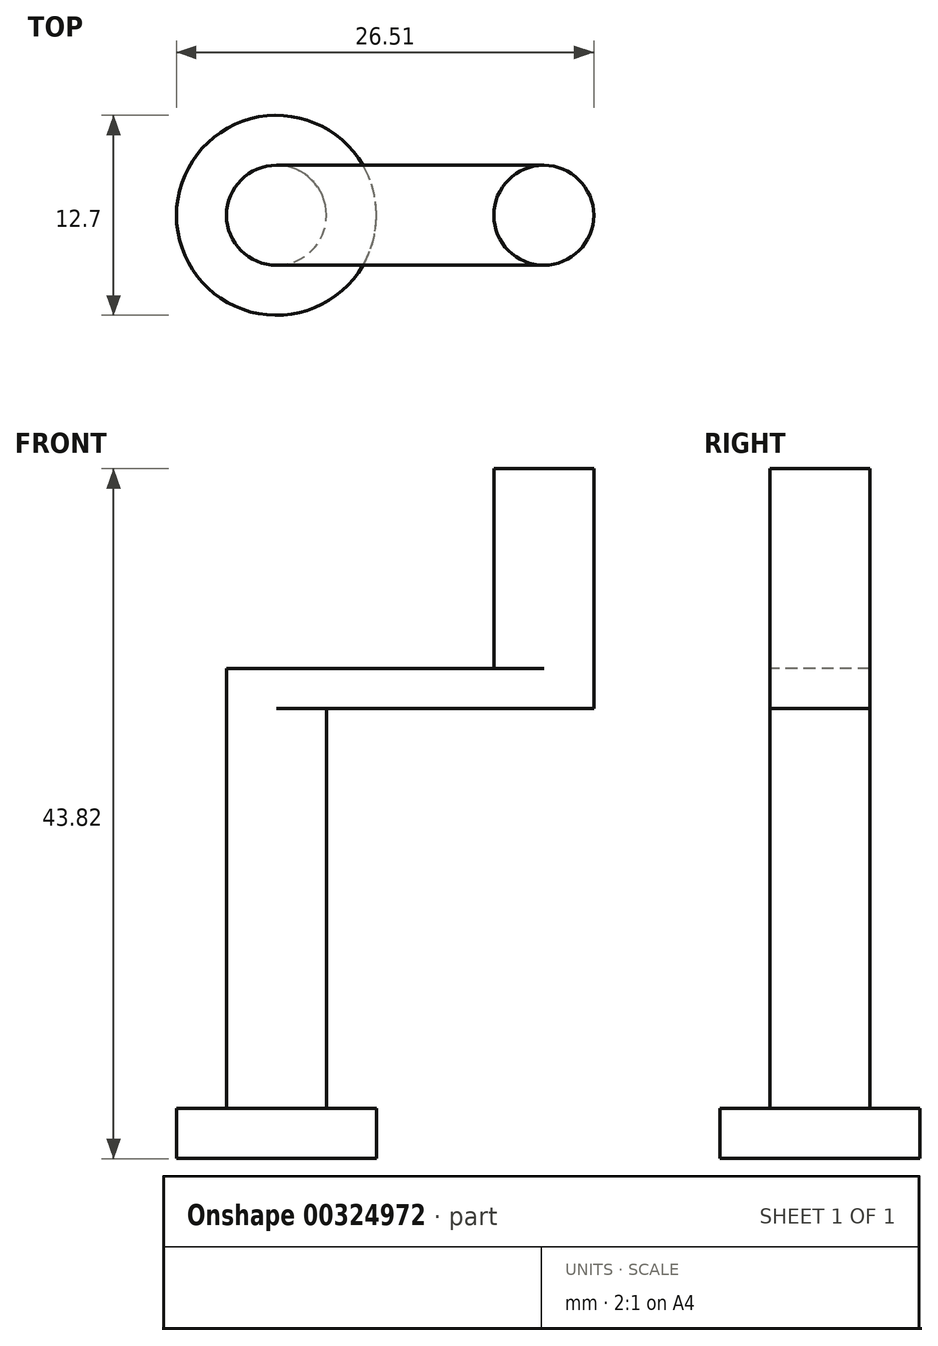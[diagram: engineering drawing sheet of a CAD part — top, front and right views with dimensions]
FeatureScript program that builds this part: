
annotation { "Feature Type Name" : "Feature", "Feature Type Description" : "" }
export const myFeature = defineFeature(function(context is Context, id is Id, definition is map)
    precondition{}
    {
        {
            var Q0;
            Q0=qCreatedBy(makeId("Top.planeOp"),FACE);
            var sketch = newSketch(context, id + "F0", { "sketchPlane" : qUnion([Q0])});
            skCircle(sketch, "E0", {"center": v(0, 0) * mm, "radius": 3.18 * mm});
            skSolve(sketch);
        }
        {
            var Q0;
            Q0 = qSketchRegion(id + "F0", true);
            extrude(context, id + "F1", {"entities" : qUnion([Q0]), "endBound" : BoundingType.SYMMETRIC, "depth" : 25.4 * mm});
        }
        {
            var Q0;
            Q0=makeQuery(id+"F1.opExtrude","CAP_FACE",FACE,{"disambiguationData":[OSD([sQuery(id+"F0.wireOp",EDGE,"E0")])],"isStart":true});
            var sketch = newSketch(context, id + "F2", { "sketchPlane" : qUnion([Q0])});
            skCircle(sketch, "E1", {"center": v(0, 0) * mm, "radius": 6.35 * mm});
            skSolve(sketch);
        }
        {
            var Q0;
            Q0 = qSketchRegion(id + "F2", true);
            extrude(context, id + "F3", {"entities" : qUnion([Q0]), "operationType" : NewBodyOperationType.ADD, "depth" : 3.17 * mm});
        }
        {
            var Q0;
            Q0=makeQuery(id+"F1.opExtrude","CAP_FACE",FACE,{"disambiguationData":[OSD([sQuery(id+"F0.wireOp",EDGE,"E0")])],"isStart":false});
            var sketch = newSketch(context, id + "F4", { "sketchPlane" : qUnion([Q0])});
            skCircle(sketch, "E2", {"center": v(16.98, 0) * mm, "radius": 3.18 * mm});
            skLineSegment(sketch, "E3", {"start": v(0, 3.18) * mm, "end": v(16.98, 3.18) * mm});
            skLineSegment(sketch, "E4", {"start": v(0, -3.17) * mm, "end": v(16.98, -3.17) * mm});
            skSolve(sketch);
        }
        {
            var Q0;
            Q0 = qSketchRegion(id + "F4", true);
            var Q1;
            {var subQ0=sQuery(id+"F4.wireOp",EDGE,"E3");Q1=makeQuery(id+"F4.imprint","IMPRINT",FACE,{"disambiguationData":[TD([[makeQuery(id+"F4.imprint","IMPRINT",EDGE,{"derivedFrom":subQ0}),-1.0]])]});}
            var Q2;
            {var subQ0=makeQuery(id+"F1.opExtrude","CAP_EDGE",EDGE,{"disambiguationData":[OSD([sQuery(id+"F0.wireOp",EDGE,"E0")])],"isStart":false});var subQ1=makeQuery(id+"F4.imprint","INTERSECT",VERTEX,{"derivedFrom":[subQ0,sQuery(id+"F4.wireOp",EDGE,"E3")]});Q2=makeQuery(id+"F4.imprint","IMPRINT",FACE,{"disambiguationData":[TD([[makeQuery(id+"F4.imprint","IMPRINT",EDGE,{"disambiguationData":[TD([[subQ1,-1.0]])],"derivedFrom":subQ0}),1.0]])]});}
            extrude(context, id + "F5", {"entities" : qUnion([Q0, Q1, Q2]), "operationType" : NewBodyOperationType.ADD, "depth" : 2.54 * mm});
        }
        {
            var Q0;
            Q0=makeQuery(id+"F5.opExtrude","CAP_FACE",FACE,{"disambiguationData":[OSD([sQuery(id+"F0.wireOp",EDGE,"E0"),sQuery(id+"F4.wireOp",EDGE,"E2"),sQuery(id+"F4.wireOp",EDGE,"E3"),sQuery(id+"F4.wireOp",EDGE,"E4")])],"isStart":false});
            var sketch = newSketch(context, id + "F6", { "sketchPlane" : qUnion([Q0])});
            skCircle(sketch, "E5", {"center": v(16.98, 0) * mm, "radius": 3.18 * mm});
            skSolve(sketch);
        }
        {
            var Q0;
            Q0 = qSketchRegion(id + "F6", true);
            extrude(context, id + "F7", {"entities" : qUnion([Q0]), "operationType" : NewBodyOperationType.ADD, "depth" : 12.7 * mm});
        }
    });
